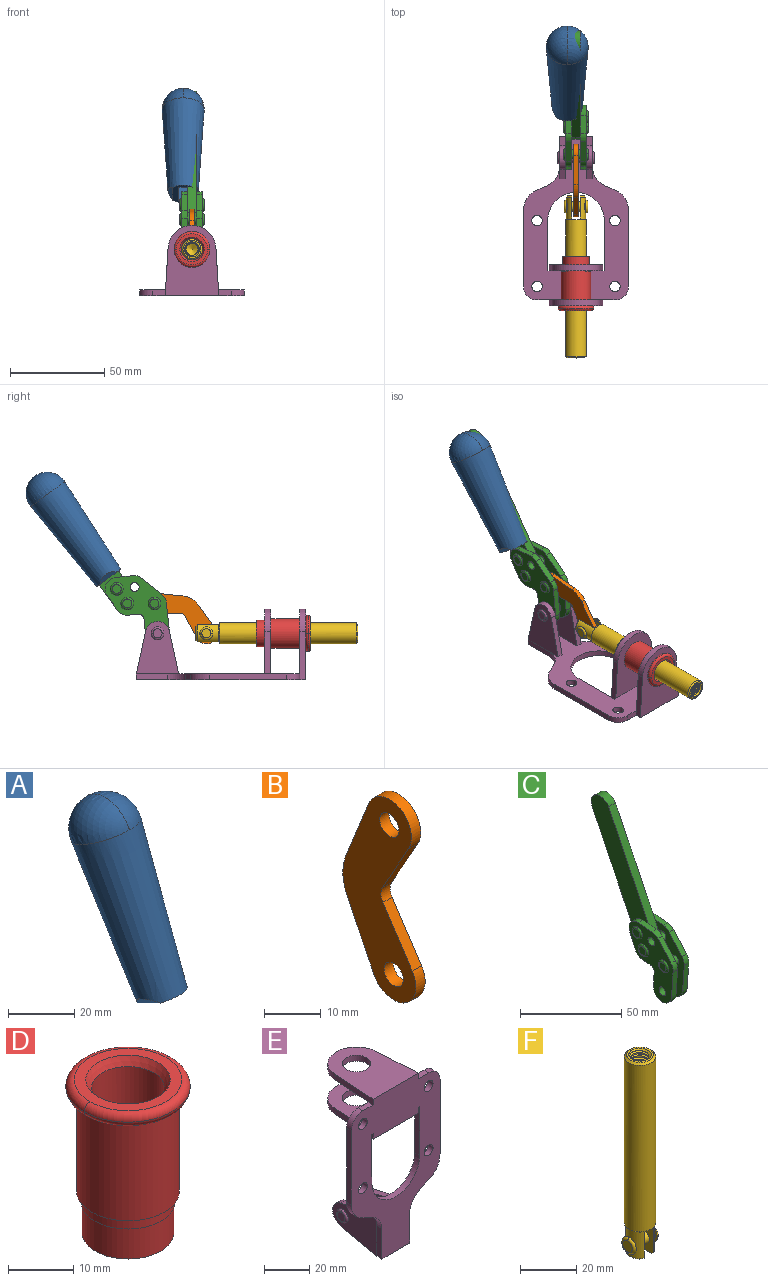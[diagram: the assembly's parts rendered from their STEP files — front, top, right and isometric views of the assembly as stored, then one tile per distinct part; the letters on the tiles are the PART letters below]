
ASSEMBLY  parts=6 mates=6
PART A: 11 faces, bbox 22.3x42.6x64.5 mm
  f0: sphere r=11.13mm, area 411.4mm2, adj f1,f8
  f1: cone r=11.11mm half-angle=3.3deg, axis (0,0.44,0.9), area 3251.8mm2, adj f0,f7,f8,f9,f10
  f2: cylinder r=6.16mm len=11.7mm, axis (1,0,0), area 89.5mm2, adj f3,f4,f5,f6
  f3: plane 60.23x36.75mm, normal (-1,0,0), area 763.6mm2, adj f2,f4,f6,f10
  f4: plane 51.37x25.05mm, normal (0,0.9,-0.44), area 264.2mm2, adj f2,f3,f5,f10
  f5: plane 60.23x36.75mm, normal (1,0,0), area 763.6mm2, adj f2,f4,f6,f10
  f6: plane 51.37x25.05mm, normal (0,-0.9,0.44), area 264.2mm2, adj f2,f3,f5,f10
  f7: plane 9.95x5.95mm, normal (0.71,-0.31,-0.64), area 25.8mm2, adj f1,f10
  f8: sphere r=11.13mm, area 411.4mm2, adj f0,f1
  f9: plane 9.95x5.95mm, normal (-0.71,-0.31,-0.64), area 25.8mm2, adj f1,f10
  f10: plane 14.27x11.38mm, normal (0,-0.44,-0.9), area 106.7mm2, adj f1,f3,f4,f5,f6,f7,f9
PART B: 12 faces, bbox 2.3x18.2x42.8 mm
  f0: cylinder r=2.4mm len=4.8mm, axis (1,0,0), area 34.9mm2, adj f4,f11
  f1: cylinder r=10.41mm len=8.47mm, axis (1,0,0), area 20.2mm2, adj f4,f9,f10,f11
  f2: cylinder r=3.05mm len=3.16mm, axis (1,0,0), area 7.7mm2, adj f4,f6,f7,f11
  f3: cylinder r=2.4mm len=4.8mm, axis (1,0,0), area 34.9mm2, adj f4,f11
  f4: plane 42.81x18.23mm, normal (-1,0,0), area 414.1mm2, adj f0,f1,f2,f3,f5,f6,f7,f8
  f5: cylinder r=5.54mm len=10.67mm, axis (1,0,0), area 41.8mm2, adj f4,f6,f10,f11
  f6: plane 11.66x6.53mm, normal (0,-0.87,-0.49), area 30.9mm2, adj f2,f4,f5,f11
  f7: plane 11.17x7.33mm, normal (0,-0.84,0.55), area 30.9mm2, adj f2,f4,f8,f11
  f8: cylinder r=5.54mm len=10.51mm, axis (1,0,0), area 41.8mm2, adj f4,f7,f9,f11
  f9: plane 13.67x6.67mm, normal (0,0.9,-0.44), area 35.1mm2, adj f1,f4,f8,f11
  f10: plane 14.1x5.7mm, normal (0,0.93,0.37), area 35.1mm2, adj f1,f4,f5,f11
  f11: plane 42.81x18.23mm, normal (1,0,0), area 414.1mm2, adj f0,f1,f2,f3,f5,f6,f7,f8
PART C: 59 faces, bbox 12.9x60.2x99.6 mm
  f0: torus R=2.39mm, axis (-1,0,0), area 14.9mm2, adj f20,f43,f51
  f1: torus R=2.39mm, axis (-1,0,0), area 14.9mm2, adj f19,f42,f51
  f2: torus R=2.39mm, axis (-1,0,0), area 14.9mm2, adj f18,f35,f51
  f3: torus R=2.39mm, axis (-1,0,0), area 14.9mm2, adj f14,f17,f23
  f4: torus R=2.39mm, axis (-1,0,0), area 14.9mm2, adj f13,f16,f23
  f5: torus R=2.39mm, axis (-1,0,0), area 14.9mm2, adj f12,f15,f23
  f6: cylinder r=2.39mm len=4.78mm, axis (1,0,0), area 46.5mm2, adj f48,f50,f51
  f7: cylinder r=2.39mm len=4.78mm, axis (1,0,0), area 46.5mm2, adj f50,f51
  f8: cylinder r=6.35mm len=12.68mm, axis (1,0,0), area 61.8mm2, adj f38,f39,f50,f51
  f9: cylinder r=2.39mm len=4.78mm, axis (-1,0,0), area 70.5mm2, adj f46,f50
  f10: cylinder r=2.39mm len=4.78mm, axis (-1,0,0), area 46.5mm2, adj f23,f45,f46
  f11: cylinder r=2.39mm len=4.78mm, axis (-1,0,0), area 46.5mm2, adj f23,f46
  f12: plane 4.78x4.78mm, normal (1,0,0), area 17.9mm2, adj f5,f15
  f13: plane 4.78x4.78mm, normal (1,0,0), area 17.9mm2, adj f4,f16
  f14: plane 4.78x4.78mm, normal (1,0,0), area 17.9mm2, adj f3,f17
  f15: torus R=2.39mm, axis (-1,0,0), area 14.9mm2, adj f5,f12,f23
  f16: torus R=2.39mm, axis (-1,0,0), area 14.9mm2, adj f4,f13,f23
  f17: torus R=2.39mm, axis (-1,0,0), area 14.9mm2, adj f3,f14,f23
  f18: plane 4.78x4.78mm, normal (-1,0,0), area 17.9mm2, adj f2,f35
  f19: plane 4.78x4.78mm, normal (-1,0,0), area 17.9mm2, adj f1,f42
  f20: plane 4.78x4.78mm, normal (-1,0,0), area 17.9mm2, adj f0,f43
  f21: plane 2.26x0.2mm, normal (1,0,0), area 0.2mm2, adj f31,f44
  f22: plane 2.26x0.2mm, normal (-1,0,0), area 0.2mm2, adj f41,f44
  f23: plane 39.37x30.77mm, normal (1,0,0), area 565.5mm2, adj f3,f4,f5,f10,f11,f15,f16,f17
  f24: cylinder r=6.1mm len=4.15mm, axis (-1,0,0), area 14.7mm2, adj f23,f25,f32,f46
  f25: plane 10.25x9.01mm, normal (0,-0.75,0.66), area 42.3mm2, adj f23,f24,f26,f46
  f26: cylinder r=6.35mm len=4.64mm, axis (-1,0,0), area 15.6mm2, adj f23,f25,f27,f46
  f27: plane 15.84x3.1mm, normal (0,-1,-0.07), area 49.2mm2, adj f23,f26,f28,f46
  f28: cylinder r=6.35mm len=12.68mm, axis (-1,0,0), area 61.8mm2, adj f23,f27,f29,f46
  f29: plane 8.11x3.1mm, normal (0,1,0.07), area 25.2mm2, adj f23,f28,f30,f46
  f30: cylinder r=3.05mm len=3.25mm, axis (-1,0,0), area 14.8mm2, adj f23,f29,f31,f46
  f31: plane 5.99x3.1mm, normal (0,0.07,-1), area 18.6mm2, adj f21,f23,f30,f44,f46
  f32: plane 9.5x3.1mm, normal (0,-0.07,1), area 29.5mm2, adj f23,f24,f33,f46,f47
  f33: cylinder r=6.1mm len=8.63mm, axis (-1,0,0), area 39.1mm2, adj f23,f32,f34,f47
  f34: plane 8.65x3.96mm, normal (0,0.91,-0.42), area 29.5mm2, adj f23,f33,f44,f47
  f35: torus R=2.39mm, axis (-1,0,0), area 14.9mm2, adj f2,f18,f51
  f36: plane 10.25x9.01mm, normal (0,-0.75,0.66), area 42.3mm2, adj f37,f49,f50,f51
  f37: cylinder r=6.35mm len=4.64mm, axis (1,0,0), area 15.6mm2, adj f36,f38,f50,f51
  f38: plane 15.84x3.1mm, normal (0,-1,-0.07), area 49.2mm2, adj f8,f37,f50,f51
  f39: plane 8.11x3.1mm, normal (0,1,0.07), area 25.2mm2, adj f8,f40,f50,f51
  f40: cylinder r=3.05mm len=3.25mm, axis (1,0,0), area 14.8mm2, adj f39,f41,f50,f51
  f41: plane 5.99x3.1mm, normal (0,0.07,-1), area 18.6mm2, adj f22,f40,f44,f50,f51
  f42: torus R=2.39mm, axis (-1,0,0), area 14.9mm2, adj f1,f19,f51
  f43: torus R=2.39mm, axis (-1,0,0), area 14.9mm2, adj f0,f20,f51
  f44: cylinder r=6.35mm len=12.12mm, axis (-1,0,0), area 128.9mm2, adj f21,f22,f23,f31,f34,f41,f46,f47
  f45: plane 2.65x1.35mm, normal (1,0,0), area 1mm2, adj f10,f55
  f46: plane 39.08x20.42mm, normal (-1,0,0), area 412.5mm2, adj f9,f10,f11,f24,f25,f26,f27,f28
  f47: plane 77.62x39.82mm, normal (1,0,0), area 850mm2, adj f32,f33,f34,f44,f53,f54,f55
  f48: plane 2.65x1.35mm, normal (-1,0,0), area 1mm2, adj f6,f55
  f49: cylinder r=6.1mm len=4.15mm, axis (1,0,0), area 14.7mm2, adj f36,f50,f51,f56
  f50: plane 39.08x20.42mm, normal (1,0,0), area 412.5mm2, adj f6,f7,f8,f9,f36,f37,f38,f39
  f51: plane 39.37x30.77mm, normal (-1,0,0), area 565.5mm2, adj f0,f1,f2,f6,f7,f8,f35,f36
  f52: plane 8.65x3.96mm, normal (0,0.91,-0.42), area 29.5mm2, adj f44,f51,f57,f58
  f53: plane 68.49x33.4mm, normal (0,0.9,-0.44), area 358.1mm2, adj f44,f47,f54,f58
  f54: cylinder r=6.35mm len=12.06mm, axis (1,0,0), area 93.7mm2, adj f47,f53,f55,f58
  f55: plane 68.49x33.4mm, normal (0,-0.9,0.44), area 358.1mm2, adj f44,f45,f46,f47,f48,f50,f54,f58
  f56: plane 9.5x3.1mm, normal (0,-0.07,1), area 29.5mm2, adj f49,f50,f51,f57,f58
  f57: cylinder r=6.1mm len=8.63mm, axis (1,0,0), area 39.1mm2, adj f51,f52,f56,f58
  f58: plane 77.62x39.82mm, normal (-1,0,0), area 850mm2, adj f44,f52,f53,f54,f55,f56,f57
PART D: 15 faces, bbox 20.6x20.6x28.7 mm
  f0: torus R=8.26mm, axis (0,0,1), area 56.8mm2, adj f1,f10,f12
  f1: torus R=8.26mm, axis (0,0,1), area 56.8mm2, adj f0,f6,f13
  f2: cylinder r=5.59mm len=25.91mm, axis (0,0,1), area 909.6mm2, adj f3,f4
  f3: cone r=6.86mm half-angle=45deg, axis (0,0,-1), area 70.2mm2, adj f2,f14
  f4: cone r=6.47mm half-angle=30deg, axis (0,0,1), area 66.7mm2, adj f2,f13
  f5: cylinder r=7.04mm len=14.07mm, axis (0,0,1), area 252.6mm2, adj f11,f14
  f6: torus R=8.26mm, axis (0,0,1), area 56.8mm2, adj f1,f12,f13
  f7: cylinder r=7.16mm len=14.33mm, axis (0,0,1), area 91.5mm2, adj f9,f11
  f8: cylinder r=7.86mm len=18.42mm, axis (0,0,1), area 909.6mm2, adj f9,f10
  f9: plane 15.72x15.72mm, normal (0,0,-1), area 33mm2, adj f7,f8
  f10: plane 16.51x16.51mm, normal (0,0,-1), area 19.9mm2, adj f0,f8,f12
  f11: plane 14.33x14.33mm, normal (0,0,-1), area 5.7mm2, adj f5,f7
  f12: torus R=8.26mm, axis (0,0,1), area 56.8mm2, adj f0,f6,f10
  f13: plane 16.51x16.51mm, normal (0,0,1), area 82.7mm2, adj f1,f4,f6
  f14: plane 14.07x14.07mm, normal (0,0,-1), area 7.8mm2, adj f3,f5
PART E: 55 faces, bbox 55.7x37.4x89.8 mm
  f0: torus R=2.41mm, axis (-1,0,0), area 15mm2, adj f11,f15,f25
  f1: torus R=2.41mm, axis (-1,0,0), area 15mm2, adj f10,f12,f22
  f2: cylinder r=2.78mm len=5.56mm, axis (0,-1,0), area 54.2mm2, adj f30,f54
  f3: cylinder r=14.99mm len=29.97mm, axis (0,-1,0), area 145.9mm2, adj f30,f49,f53,f54
  f4: cylinder r=2.78mm len=5.56mm, axis (0,-1,0), area 54.2mm2, adj f30,f54
  f5: cylinder r=2.78mm len=5.56mm, axis (0,-1,0), area 54.2mm2, adj f30,f54
  f6: cylinder r=2.78mm len=5.56mm, axis (0,-1,0), area 54.2mm2, adj f30,f54
  f7: cylinder r=6.35mm len=12.7mm, axis (0,0,1), area 123.6mm2, adj f27,f51
  f8: cylinder r=6.35mm len=12.7mm, axis (0,0,-1), area 124.7mm2, adj f21,f35
  f9: cylinder r=2.41mm len=11.18mm, axis (-1,0,0), area 169.4mm2, adj f16,f19
  f10: plane 4.83x4.83mm, normal (1,0,0), area 18.3mm2, adj f1,f12
  f11: plane 4.83x4.83mm, normal (-1,0,0), area 18.3mm2, adj f0,f15
  f12: torus R=2.41mm, axis (-1,0,0), area 15mm2, adj f1,f10,f22
  f13: cylinder r=6.35mm len=12.41mm, axis (1,0,0), area 53.4mm2, adj f18,f19,f22,f23
  f14: cylinder r=6.35mm len=12.41mm, axis (-1,0,0), area 53.4mm2, adj f16,f17,f24,f25
  f15: torus R=2.41mm, axis (-1,0,0), area 15mm2, adj f0,f11,f25
  f16: plane 27.86x22.35mm, normal (1,0,0), area 425.4mm2, adj f9,f14,f17,f24,f30
  f17: plane 22.86x4.97mm, normal (0,0.21,0.98), area 72.5mm2, adj f14,f16,f25,f30
  f18: plane 22.86x4.97mm, normal (0,0.21,0.98), area 72.5mm2, adj f13,f19,f22,f30
  f19: plane 27.86x22.35mm, normal (-1,0,0), area 425.4mm2, adj f9,f13,f18,f23,f30
  f20: cylinder r=12.7mm len=25.35mm, axis (0,0,-1), area 119.8mm2, adj f21,f34,f35,f36
  f21: plane 34.21x28.07mm, normal (0,0,-1), area 702.4mm2, adj f8,f20,f30,f34,f36
  f22: plane 27.96x22.45mm, normal (1,0,0), area 407.2mm2, adj f1,f12,f13,f18,f23,f30,f42,f43
  f23: plane 22.86x4.97mm, normal (0,0.21,-0.98), area 72.5mm2, adj f13,f19,f22,f44
  f24: plane 22.86x4.97mm, normal (0,0.21,-0.98), area 72.5mm2, adj f14,f16,f25,f44
  f25: plane 27.86x22.35mm, normal (-1,0,0), area 407.1mm2, adj f0,f14,f15,f17,f24,f30,f45,f46
  f26: plane 3.1x0.95mm, normal (0,0,-1), area 2.7mm2, adj f30,f49,f50,f54
  f27: plane 34.21x28.07mm, normal (0,0,1), area 702.4mm2, adj f7,f28,f30,f50,f52
  f28: cylinder r=12.7mm len=25.35mm, axis (0,0,1), area 118.8mm2, adj f27,f50,f51,f52
  f29: plane 3.1x0.95mm, normal (0,0,-1), area 2.7mm2, adj f30,f52,f53,f54
  f30: plane 86.54x55.63mm, normal (0,1,0), area 2362.9mm2, adj f2,f3,f4,f5,f6,f16,f17,f18
  f31: plane 40.56x3.1mm, normal (-1,0,0), area 125.7mm2, adj f30,f32,f48,f54
  f32: cylinder r=7.11mm len=7.11mm, axis (0,-1,0), area 34.6mm2, adj f30,f31,f33,f54
  f33: plane 6.67x3.1mm, normal (0,0,1), area 20.4mm2, adj f30,f32,f34,f54
  f34: plane 25.39x3.13mm, normal (-1,0.06,0), area 79.5mm2, adj f20,f21,f33,f35,f54
  f35: plane 37.31x28.45mm, normal (0,0,1), area 789.9mm2, adj f8,f20,f34,f36,f54
  f36: plane 25.39x3.13mm, normal (1,0.06,0), area 79.5mm2, adj f20,f21,f35,f37,f54
  f37: plane 6.67x3.1mm, normal (0,0,1), area 20.4mm2, adj f30,f36,f38,f54
  f38: cylinder r=7.11mm len=7.11mm, axis (0,-1,0), area 34.6mm2, adj f30,f37,f39,f54
  f39: plane 40.56x3.1mm, normal (1,0,0), area 125.7mm2, adj f30,f38,f40,f54
  f40: cylinder r=11.18mm len=10.16mm, axis (0,-1,0), area 39.5mm2, adj f30,f39,f41,f54
  f41: plane 6.09x3.1mm, normal (0.42,0,-0.91), area 20.8mm2, adj f30,f40,f42,f54
  f42: cylinder r=11.18mm len=9.41mm, axis (0,-1,0), area 37.2mm2, adj f22,f30,f41,f43,f54
  f43: plane 16.5x3.1mm, normal (1,0,0), area 51.1mm2, adj f22,f42,f44,f54
  f44: plane 17.37x3.1mm, normal (0,0,-1), area 53.8mm2, adj f23,f24,f30,f43,f45,f54
  f45: plane 16.5x3.1mm, normal (-1,0,0), area 51.1mm2, adj f25,f44,f46,f54
  f46: cylinder r=11.18mm len=9.41mm, axis (0,-1,0), area 37.2mm2, adj f25,f30,f45,f47,f54
  f47: plane 6.09x3.1mm, normal (-0.42,0,-0.91), area 20.8mm2, adj f30,f46,f48,f54
  f48: cylinder r=11.18mm len=10.16mm, axis (0,-1,0), area 39.5mm2, adj f30,f31,f47,f54
  f49: plane 26.54x3.1mm, normal (-1,0,0), area 82.3mm2, adj f3,f26,f30,f54
  f50: plane 25.39x3.1mm, normal (1,0.06,0), area 78.8mm2, adj f26,f27,f28,f51,f54
  f51: plane 37.31x28.45mm, normal (0,0,-1), area 789.9mm2, adj f7,f28,f50,f52,f54
  f52: plane 25.39x3.1mm, normal (-1,0.06,0), area 78.8mm2, adj f27,f28,f29,f51,f54
  f53: plane 26.54x3.1mm, normal (1,0,0), area 82.3mm2, adj f3,f29,f30,f54
  f54: plane 89.66x55.63mm, normal (0,-1,0), area 2678.5mm2, adj f2,f3,f4,f5,f6,f26,f29,f31
PART F: 48 faces, bbox 12.6x11.1x86.1 mm
  f0: torus R=2.41mm, axis (-1,0,0), area 15mm2, adj f30,f32,f34
  f1: torus R=2.41mm, axis (-1,0,0), area 15mm2, adj f29,f31,f33
  f2: cylinder r=5.54mm len=72.39mm, axis (0,0,1), area 2518.5mm2, adj f3,f4,f42,f43
  f3: cone r=5.54mm half-angle=45deg, axis (0,0,1), area 7.6mm2, adj f2,f5,f41
  f4: cone r=5.54mm half-angle=45deg, axis (0,0,-1), area 34.9mm2, adj f2,f39
  f5: cylinder r=5.08mm len=11.48mm, axis (0,0,1), area 108.3mm2, adj f3,f7,f8,f41
  f6: cylinder r=2.41mm len=4.83mm, axis (-1,0,0), area 71.2mm2, adj f40,f41
  f7: cylinder r=2.41mm len=4.83mm, axis (-1,0,0), area 7.6mm2, adj f5,f34
  f8: cone r=5.08mm half-angle=45deg, axis (0,0,1), area 10.6mm2, adj f5,f37,f41
  f9: cone r=3.98mm half-angle=45deg, axis (0,0,1), area 17.6mm2, adj f27,f39,f45,f46,f47
  f10: cylinder r=2.41mm len=4.83mm, axis (-1,0,0), area 7.6mm2, adj f33,f38
  f11: cylinder r=3.2mm len=6.4mm, axis (0,0,1), area 78.4mm2, adj f12,f28,f44,f45,f47
  f12: cylinder r=3.2mm len=6.4mm, axis (0,0,1), area 10.5mm2, adj f11,f13,f45,f47
  f13: cylinder r=3.2mm len=6.4mm, axis (0,0,1), area 10.5mm2, adj f12,f14,f45,f47
  f14: cylinder r=3.2mm len=6.4mm, axis (0,0,1), area 10.5mm2, adj f13,f15,f45,f47
  f15: cylinder r=3.2mm len=6.4mm, axis (0,0,1), area 10.5mm2, adj f14,f16,f45,f47
  f16: cylinder r=3.2mm len=6.4mm, axis (0,0,1), area 10.5mm2, adj f15,f17,f45,f47
  f17: cylinder r=3.2mm len=6.4mm, axis (0,0,1), area 10.5mm2, adj f16,f18,f45,f47
  f18: cylinder r=3.2mm len=6.4mm, axis (0,0,1), area 10.5mm2, adj f17,f19,f45,f47
  f19: cylinder r=3.2mm len=6.4mm, axis (0,0,1), area 10.5mm2, adj f18,f20,f45,f47
  f20: cylinder r=3.2mm len=6.4mm, axis (0,0,1), area 10.5mm2, adj f19,f21,f45,f47
  f21: cylinder r=3.2mm len=6.4mm, axis (0,0,1), area 10.5mm2, adj f20,f22,f45,f47
  f22: cylinder r=3.2mm len=6.4mm, axis (0,0,1), area 10.5mm2, adj f21,f23,f45,f47
  f23: cylinder r=3.2mm len=6.4mm, axis (0,0,1), area 10.5mm2, adj f22,f24,f45,f47
  f24: cylinder r=3.2mm len=6.4mm, axis (0,0,1), area 10.5mm2, adj f23,f25,f45,f47
  f25: cylinder r=3.2mm len=6.4mm, axis (0,0,1), area 10.5mm2, adj f24,f26,f45,f47
  f26: cylinder r=3.2mm len=6.4mm, axis (0,0,1), area 10.5mm2, adj f25,f27,f45,f47
  f27: cylinder r=3.2mm len=6.4mm, axis (0,0,1), area 7.4mm2, adj f9,f26,f45,f47
  f28: cone r=3.2mm half-angle=60deg, axis (0,0,1), area 37.2mm2, adj f11
  f29: plane 4.83x4.83mm, normal (-1,0,0), area 18.3mm2, adj f1,f31
  f30: plane 4.83x4.83mm, normal (1,0,0), area 18.3mm2, adj f0,f32
  f31: torus R=2.41mm, axis (-1,0,0), area 15mm2, adj f1,f29,f33
  f32: torus R=2.41mm, axis (-1,0,0), area 15mm2, adj f0,f30,f34
  f33: plane 6.83x6.83mm, normal (1,0,0), area 18.3mm2, adj f1,f10,f31
  f34: plane 6.83x6.83mm, normal (-1,0,0), area 18.3mm2, adj f0,f7,f32
  f35: cone r=5.08mm half-angle=45deg, axis (0,0,1), area 10.6mm2, adj f36,f38,f40
  f36: plane 7.25x1.97mm, normal (0,0,-1), area 10mm2, adj f35,f40
  f37: plane 7.25x1.97mm, normal (0,0,-1), area 10mm2, adj f8,f41
  f38: cylinder r=5.08mm len=11.48mm, axis (0,0,1), area 108.3mm2, adj f10,f35,f40,f42
  f39: plane 9.55x9.55mm, normal (0,0,1), area 22mm2, adj f4,f9
  f40: plane 12.76x10.09mm, normal (1,0,0), area 95.7mm2, adj f6,f35,f36,f38,f42,f43
  f41: plane 12.76x10.09mm, normal (-1,0,0), area 95.7mm2, adj f3,f5,f6,f8,f37,f43
  f42: cone r=5.54mm half-angle=45deg, axis (0,0,1), area 7.6mm2, adj f2,f38,f40
  f43: plane 11.07x4.7mm, normal (0,0,-1), area 50.4mm2, adj f2,f40,f41
  f44: plane 0.89x0.62mm, normal (-1,0,0), area 0.3mm2, adj f11,f45,f46,f47
  f45: bspline ~24.8x7.63mm, area 266.6mm2, adj f9,f11,f12,f13,f14,f15,f16,f17
  f46: bspline ~24.87x7.63mm, area 73.6mm2, adj f9,f44,f45,f47
  f47: bspline ~24.98x7.63mm, area 272.5mm2, adj f9,f11,f12,f13,f14,f15,f16,f17
PLACE A rot(axis=(-1,0,0),10deg) t=(-4.66,21.5,58.58)mm
PLACE B rot(axis=(1,0,0),121.8deg) t=(0,41.76,11.86)mm
PLACE C rot(axis=(-1,0,0),10deg) t=(0,22.86,60.49)mm
PLACE D rot(axis=(1,0,0),90deg) t=(0,9.43,0)mm
PLACE E rot(axis=(1,0,0),90deg) t=(0,9.43,0)mm fixed
PLACE F rot(axis=(1,0,0),90deg) t=(0,31.11,0)mm
MATE slider E.f7 <-> F.f2  axis (0,-1,0) through (0,-36.96,24.61)mm
MATE revolute E.f0 <-> C.f7  axis (-1,0,0) through (0,41.52,24.61)mm
MATE revolute F.f6 <-> B.f5  axis (-1,0,0) through (0,15.64,24.61)mm
MATE fastened D.f2 <-> E.f7  axis (0,1,0) through (0,-36.96,24.61)mm
MATE revolute C.f4 <-> B.f3  axis (-1,0,0) through (0,43.18,40.4)mm
MATE fastened A.f3 <-> C.f58  axis (-1,0,0) through (-2.35,85.61,79.04)mm
